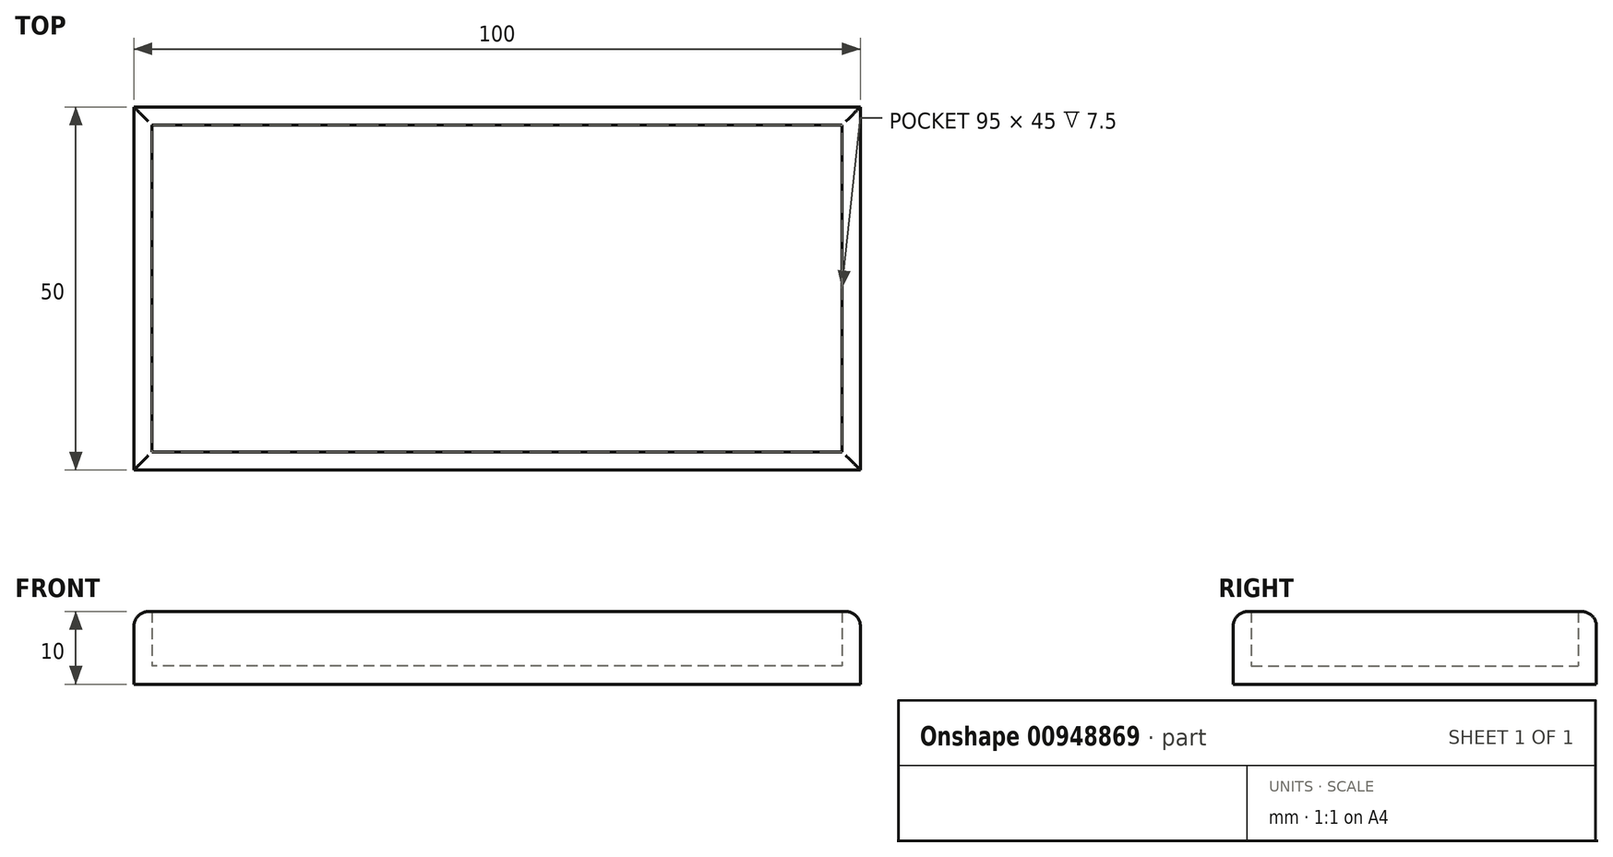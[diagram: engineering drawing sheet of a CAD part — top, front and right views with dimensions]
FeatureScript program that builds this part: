
annotation { "Feature Type Name" : "Feature", "Feature Type Description" : "" }
export const myFeature = defineFeature(function(context is Context, id is Id, definition is map)
    precondition{}
    {
        {
            var Q0;
            Q0=qCreatedBy(makeId("Top.planeOp"),FACE);
            var sketch = newSketch(context, id + "F0", { "sketchPlane" : qUnion([Q0])});
            skLineSegment(sketch, "E0.bottom", {"start": v(50, -25) * mm, "end": v(-50, -25) * mm});
            skLineSegment(sketch, "E0.top", {"start": v(50, 25) * mm, "end": v(-50, 25) * mm});
            skLineSegment(sketch, "E0.left", {"start": v(50, -25) * mm, "end": v(50, 25) * mm});
            skLineSegment(sketch, "E0.right", {"start": v(-50, -25) * mm, "end": v(-50, 25) * mm});
            skPoint(sketch, "E0.middle", {"position": v(0, 0) * mm});
            skSolve(sketch);
        }
        {
            var Q0;
            Q0=makeQuery(id+"F0.imprint","IMPRINT",FACE,{"disambiguationData":[TD([[makeQuery(id+"F0.imprint","IMPRINT",EDGE,{"derivedFrom":sQuery(id+"F0.wireOp",EDGE,"E0.bottom")}),-1.0]])]});
            extrude(context, id + "F1", {"entities" : qUnion([Q0]), "depth" : 10 * mm, "offsetDistance" : 25 * mm});
        }
        {
            var Q0;
            Q0=makeQuery(id+"F1.opExtrude","CAP_FACE",FACE,{"disambiguationData":[OSD([sQuery(id+"F0.wireOp",EDGE,"E0.bottom"),sQuery(id+"F0.wireOp",EDGE,"E0.top"),sQuery(id+"F0.wireOp",EDGE,"E0.left"),sQuery(id+"F0.wireOp",EDGE,"E0.right")])],"isStart":false});
            fillet(context, id + "F2", {"entities" : qUnion([Q0]), "radius" : 2 * mm, "tangentPropagation" : true, "allowEdgeOverflow" : false});
        }
        {
            var Q0;
            Q0=makeQuery(id+"F1.opExtrude","CAP_FACE",FACE,{"disambiguationData":[OSD([sQuery(id+"F0.wireOp",EDGE,"E0.bottom"),sQuery(id+"F0.wireOp",EDGE,"E0.top"),sQuery(id+"F0.wireOp",EDGE,"E0.left"),sQuery(id+"F0.wireOp",EDGE,"E0.right")])],"isStart":false});
            shell(context, id + "F3", {"entities" : qUnion([Q0]), "thickness" : 2.5 * mm});
        }
    });
